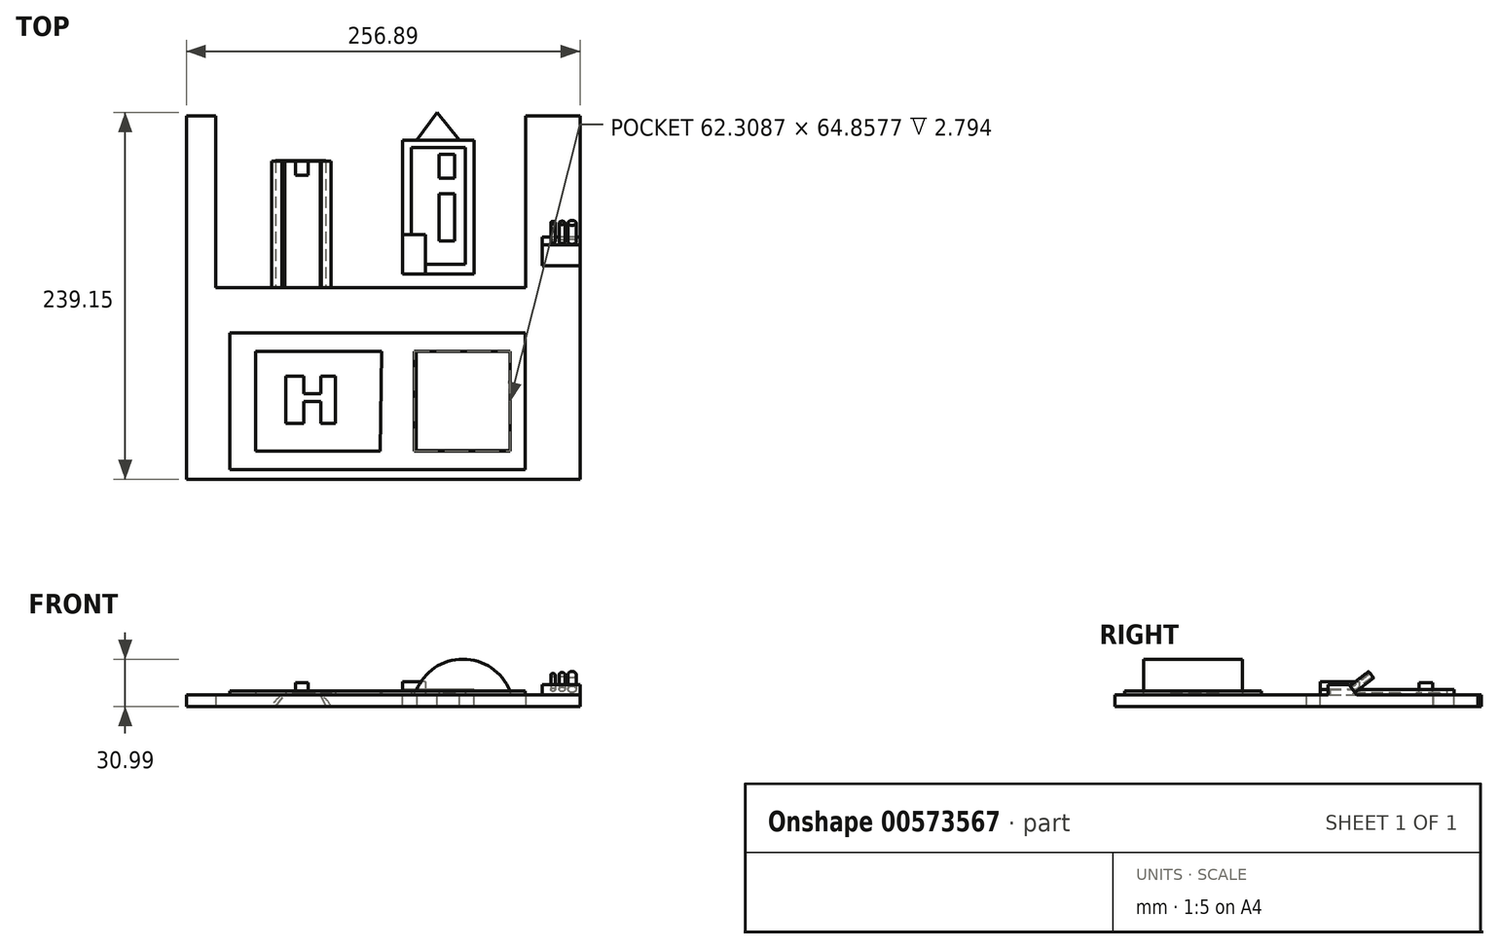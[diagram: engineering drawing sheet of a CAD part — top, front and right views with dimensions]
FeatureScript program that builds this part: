
annotation { "Feature Type Name" : "Feature", "Feature Type Description" : "" }
export const myFeature = defineFeature(function(context is Context, id is Id, definition is map)
    precondition{}
    {
        {
            var Q0;
            Q0=qCreatedBy(makeId("Top.planeOp"),FACE);
            var sketch = newSketch(context, id + "F0", { "sketchPlane" : qUnion([Q0])});
            skLineSegment(sketch, "E0.bottom", {"start": v(-141.19, 57.64) * mm, "end": v(115.7, 57.64) * mm});
            skLineSegment(sketch, "E0.top", {"start": v(-141.19, -67.27) * mm, "end": v(115.7, -67.27) * mm});
            skLineSegment(sketch, "E0.left", {"start": v(-141.19, 57.64) * mm, "end": v(-141.19, -67.27) * mm});
            skLineSegment(sketch, "E0.right", {"start": v(115.7, 57.64) * mm, "end": v(115.7, -67.27) * mm});
            skSolve(sketch);
        }
        {
            var Q0;
            Q0 = qSketchRegion(id + "F0", true);
            extrude(context, id + "F1", {"entities" : qUnion([Q0]), "depth" : 7.37 * mm, "offsetDistance" : 25.4 * mm});
        }
        {
            var Q0;
            Q0=makeQuery(id+"F1.opExtrude","CAP_FACE",FACE,{"disambiguationData":[OSD([sQuery(id+"F0.wireOp",EDGE,"E0.bottom"),sQuery(id+"F0.wireOp",EDGE,"E0.top"),sQuery(id+"F0.wireOp",EDGE,"E0.left"),sQuery(id+"F0.wireOp",EDGE,"E0.right")])],"isStart":false});
            var sketch = newSketch(context, id + "F2", { "sketchPlane" : qUnion([Q0])});
            skLineSegment(sketch, "E1", {"start": v(-13.88, 16) * mm, "end": v(-96.01, 16) * mm});
            skLineSegment(sketch, "E2", {"start": v(-96.01, 16) * mm, "end": v(-96.01, -48.86) * mm});
            skLineSegment(sketch, "E3", {"start": v(-96.01, -48.86) * mm, "end": v(-14.73, -48.86) * mm});
            skLineSegment(sketch, "E4", {"start": v(-14.73, -48.86) * mm, "end": v(-13.88, 16) * mm});
            skLineSegment(sketch, "E5", {"start": v(-13.88, -61.03) * mm, "end": v(-112.72, -61.03) * mm});
            skLineSegment(sketch, "E6", {"start": v(-112.72, -61.03) * mm, "end": v(-112.72, 28.18) * mm});
            skLineSegment(sketch, "E7", {"start": v(-112.72, 28.18) * mm, "end": v(-13.88, 28.18) * mm});
            skLineSegment(sketch, "E8", {"start": v(-13.88, 28.18) * mm, "end": v(79.87, 28.18) * mm});
            skLineSegment(sketch, "E9", {"start": v(79.87, 28.18) * mm, "end": v(79.87, -61.03) * mm});
            skLineSegment(sketch, "E10", {"start": v(79.87, -61.03) * mm, "end": v(-13.88, -61.03) * mm});
            skLineSegment(sketch, "E11", {"start": v(7.65, 16) * mm, "end": v(7.65, -48.86) * mm});
            skLineSegment(sketch, "E12", {"start": v(7.65, -48.86) * mm, "end": v(69.96, -48.86) * mm});
            skLineSegment(sketch, "E13", {"start": v(69.96, -48.86) * mm, "end": v(69.96, 16) * mm});
            skLineSegment(sketch, "E14", {"start": v(69.96, 16) * mm, "end": v(7.65, 16) * mm});
            skSolve(sketch);
        }
        {
            var Q0;
            Q0 = qSketchRegion(id + "F2", true);
            extrude(context, id + "F3", {"entities" : qUnion([Q0]), "operationType" : NewBodyOperationType.ADD, "depth" : 2.8 * mm, "offsetDistance" : 25.4 * mm});
        }
        {
            var Q0;
            Q0=makeQuery(id+"F3.boolean.opBoolean","SPLIT",FACE,{"disambiguationData":[TD([makeQuery(id+"F3.opExtrude","SWEPT_FACE",FACE,{"disambiguationData":[OSD([sQuery(id+"F2.wireOp",EDGE,"E1")])]})])],"derivedFrom":makeQuery(id+"F1.opExtrude","CAP_FACE",FACE,{"disambiguationData":[OSD([sQuery(id+"F0.wireOp",EDGE,"E0.bottom"),sQuery(id+"F0.wireOp",EDGE,"E0.top"),sQuery(id+"F0.wireOp",EDGE,"E0.left"),sQuery(id+"F0.wireOp",EDGE,"E0.right")])],"isStart":false})});
            var sketch = newSketch(context, id + "F4", { "sketchPlane" : qUnion([Q0])});
            skLineSegment(sketch, "E15", {"start": v(-76.23, 0) * mm, "end": v(-76.23, -30.71) * mm});
            skLineSegment(sketch, "E16", {"start": v(-76.23, -30.71) * mm, "end": v(-64.56, -30.71) * mm});
            skLineSegment(sketch, "E17", {"start": v(-64.56, -30.71) * mm, "end": v(-64.56, -16.64) * mm});
            skLineSegment(sketch, "E18", {"start": v(-64.56, -16.64) * mm, "end": v(-53.58, -16.64) * mm});
            skLineSegment(sketch, "E19", {"start": v(-53.58, -16.64) * mm, "end": v(-53.58, -30.71) * mm});
            skLineSegment(sketch, "E20", {"start": v(-53.58, -30.71) * mm, "end": v(-43.97, -30.71) * mm});
            skLineSegment(sketch, "E21", {"start": v(-43.97, -30.71) * mm, "end": v(-43.97, 0) * mm});
            skLineSegment(sketch, "E22", {"start": v(-43.97, 0) * mm, "end": v(-53.58, 0) * mm});
            skLineSegment(sketch, "E23", {"start": v(-53.58, 0) * mm, "end": v(-53.58, -11.5) * mm});
            skLineSegment(sketch, "E24", {"start": v(-53.58, -11.5) * mm, "end": v(-64.56, -11.5) * mm});
            skLineSegment(sketch, "E25", {"start": v(-64.56, -11.5) * mm, "end": v(-64.56, 0) * mm});
            skLineSegment(sketch, "E26", {"start": v(-64.56, 0) * mm, "end": v(-76.23, 0) * mm});
            skSolve(sketch);
        }
        {
            var Q0;
            Q0 = qSketchRegion(id + "F4", true);
            extrude(context, id + "F5", {"entities" : qUnion([Q0]), "operationType" : NewBodyOperationType.ADD, "depth" : 1.78 * mm, "offsetDistance" : 25.4 * mm});
        }
        {
            var Q0;
            Q0=makeQuery(id+"F3.opExtrude","SWEPT_FACE",FACE,{"disambiguationData":[OSD([sQuery(id+"F2.wireOp",EDGE,"E14")])]});
            var sketch = newSketch(context, id + "F6", { "sketchPlane" : qUnion([Q0])});
            skArc(sketch, "E27", {"start": v(69.96, 10.16) * mm, "mid": v(37.82, 30.7) * mm, "end": v(7.65, 7.37) * mm});
            skSolve(sketch);
        }
        {
            var Q0;
            {var subQ0=sQuery(id+"F6.wireOp",EDGE,"E27");var subQ1=sQuery(id+"F2.wireOp",EDGE,"E14");var subQ2=makeQuery(id+"F3.opExtrude","CAP_EDGE",EDGE,{"disambiguationData":[OSD([subQ1])],"isStart":false});var subQ4=makeQuery(id+"F6.imprint","INTERSECT",VERTEX,{"derivedFrom":[subQ2,subQ0]});Q0=makeQuery(id+"F6.imprint","IMPRINT",FACE,{"disambiguationData":[TD([[makeQuery(id+"F6.imprint","IMPRINT",EDGE,{"disambiguationData":[TD([[subQ4,1.0]])],"derivedFrom":subQ0}),1.0]])]});}
            extrude(context, id + "F7", {"entities" : qUnion([Q0]), "depth" : 64.52 * mm, "offsetDistance" : 25.4 * mm});
        }
        {
            var Q0;
            Q0=makeQuery(id+"F1.opExtrude","SWEPT_FACE",FACE,{"disambiguationData":[OSD([sQuery(id+"F0.wireOp",EDGE,"E0.bottom")])]});
            var sketch = newSketch(context, id + "F8", { "sketchPlane" : qUnion([Q0])});
            skLineSegment(sketch, "E28.bottom", {"start": v(-80.15, 7.37) * mm, "end": v(-115.7, 7.37) * mm});
            skLineSegment(sketch, "E28.top", {"start": v(-80.15, 0) * mm, "end": v(-115.7, 0) * mm});
            skLineSegment(sketch, "E28.left", {"start": v(-80.15, 7.37) * mm, "end": v(-80.15, 0) * mm});
            skLineSegment(sketch, "E28.right", {"start": v(-115.7, 7.37) * mm, "end": v(-115.7, 0) * mm});
            skLineSegment(sketch, "E29.bottom", {"start": v(141.19, 7.37) * mm, "end": v(122.07, 7.37) * mm});
            skLineSegment(sketch, "E29.top", {"start": v(141.19, 0) * mm, "end": v(122.07, 0) * mm});
            skLineSegment(sketch, "E29.left", {"start": v(141.19, 7.37) * mm, "end": v(141.19, 0) * mm});
            skLineSegment(sketch, "E29.right", {"start": v(122.07, 7.37) * mm, "end": v(122.07, 0) * mm});
            skSolve(sketch);
        }
        {
            var Q0;
            Q0 = qSketchRegion(id + "F8", true);
            extrude(context, id + "F9", {"entities" : qUnion([Q0]), "operationType" : NewBodyOperationType.ADD, "depth" : 112.01 * mm, "offsetDistance" : 25.4 * mm});
        }
        {
            var Q0;
            {var subQ0=sQuery(id+"F0.wireOp",EDGE,"E0.left");var subQ1=sQuery(id+"F0.wireOp",EDGE,"E0.top");var subQ2=sQuery(id+"F0.wireOp",EDGE,"E0.right");var subQ3=sQuery(id+"F0.wireOp",EDGE,"E0.bottom");Q0=makeQuery(id+"F9.boolean.opBoolean","MERGE",FACE,{"derivedFrom":[makeQuery(id+"F3.boolean.opBoolean","SPLIT",FACE,{"disambiguationData":[TD([makeQuery(id+"F1.opExtrude","SWEPT_FACE",FACE,{"disambiguationData":[OSD([subQ3])]})])],"derivedFrom":makeQuery(id+"F1.opExtrude","CAP_FACE",FACE,{"disambiguationData":[OSD([subQ3,subQ1,subQ0,subQ2])],"isStart":false})}),makeQuery(id+"F9.opExtrude","SWEPT_FACE",FACE,{"disambiguationData":[OSD([sQuery(id+"F8.wireOp",EDGE,"E28.bottom")])]}),makeQuery(id+"F9.opExtrude","SWEPT_FACE",FACE,{"disambiguationData":[OSD([sQuery(id+"F8.wireOp",EDGE,"E29.bottom")])]})]});}
            var sketch = newSketch(context, id + "F10", { "sketchPlane" : qUnion([Q0])});
            skLineSegment(sketch, "E30.bottom", {"start": v(46.65, 153.87) * mm, "end": v(0, 153.87) * mm});
            skLineSegment(sketch, "E30.top", {"start": v(46.65, 66.6) * mm, "end": v(0, 66.6) * mm});
            skLineSegment(sketch, "E30.left", {"start": v(46.65, 153.87) * mm, "end": v(46.65, 66.6) * mm});
            skLineSegment(sketch, "E30.right", {"start": v(0, 153.87) * mm, "end": v(0, 66.6) * mm});
            skSolve(sketch);
        }
        {
            var Q0;
            Q0 = qSketchRegion(id + "F10", true);
            extrude(context, id + "F11", {"entities" : qUnion([Q0]), "oppositeDirection" : true, "depth" : 7.62 * mm, "offsetDistance" : 25.4 * mm});
        }
        {
            var Q0;
            Q0=makeQuery(id+"F11.opExtrude","CAP_FACE",FACE,{"disambiguationData":[OSD([sQuery(id+"F10.wireOp",EDGE,"E30.bottom"),sQuery(id+"F10.wireOp",EDGE,"E30.top"),sQuery(id+"F10.wireOp",EDGE,"E30.left"),sQuery(id+"F10.wireOp",EDGE,"E30.right")])],"isStart":true});
            var sketch = newSketch(context, id + "F12", { "sketchPlane" : qUnion([Q0])});
            skLineSegment(sketch, "E31.bottom", {"start": v(33.86, 144.73) * mm, "end": v(23.8, 144.73) * mm});
            skLineSegment(sketch, "E31.top", {"start": v(33.86, 129.2) * mm, "end": v(23.8, 129.2) * mm});
            skLineSegment(sketch, "E31.left", {"start": v(33.86, 144.73) * mm, "end": v(33.86, 129.2) * mm});
            skLineSegment(sketch, "E31.right", {"start": v(23.8, 144.73) * mm, "end": v(23.8, 129.2) * mm});
            skLineSegment(sketch, "E32.bottom", {"start": v(33.86, 119.14) * mm, "end": v(23.8, 119.14) * mm});
            skLineSegment(sketch, "E32.top", {"start": v(33.86, 88.07) * mm, "end": v(23.8, 88.07) * mm});
            skLineSegment(sketch, "E32.left", {"start": v(33.86, 119.14) * mm, "end": v(33.86, 88.07) * mm});
            skLineSegment(sketch, "E32.right", {"start": v(23.8, 119.14) * mm, "end": v(23.8, 88.07) * mm});
            skSolve(sketch);
        }
        {
            var Q0;
            Q0 = qSketchRegion(id + "F12", true);
            extrude(context, id + "F13", {"entities" : qUnion([Q0]), "operationType" : NewBodyOperationType.ADD, "depth" : 1.27 * mm, "offsetDistance" : 25.4 * mm});
        }
        {
            var Q0;
            Q0=makeQuery(id+"F11.opExtrude","CAP_FACE",FACE,{"disambiguationData":[OSD([sQuery(id+"F10.wireOp",EDGE,"E30.bottom"),sQuery(id+"F10.wireOp",EDGE,"E30.top"),sQuery(id+"F10.wireOp",EDGE,"E30.left"),sQuery(id+"F10.wireOp",EDGE,"E30.right")])],"isStart":true});
            var sketch = newSketch(context, id + "F14", { "sketchPlane" : qUnion([Q0])});
            skLineSegment(sketch, "E33.bottom", {"start": v(14.67, 66.6) * mm, "end": v(0, 66.6) * mm});
            skLineSegment(sketch, "E33.top", {"start": v(14.67, 92.19) * mm, "end": v(0, 92.19) * mm});
            skLineSegment(sketch, "E33.left", {"start": v(14.67, 66.6) * mm, "end": v(14.67, 92.19) * mm});
            skLineSegment(sketch, "E33.right", {"start": v(0, 66.6) * mm, "end": v(0, 92.19) * mm});
            skSolve(sketch);
        }
        {
            var Q0;
            Q0 = qSketchRegion(id + "F14", true);
            extrude(context, id + "F15", {"entities" : qUnion([Q0]), "operationType" : NewBodyOperationType.ADD, "depth" : 8.64 * mm, "offsetDistance" : 25.4 * mm});
        }
        {
            var Q0;
            Q0=makeQuery(id+"F11.opExtrude","CAP_FACE",FACE,{"disambiguationData":[OSD([sQuery(id+"F10.wireOp",EDGE,"E30.bottom"),sQuery(id+"F10.wireOp",EDGE,"E30.top"),sQuery(id+"F10.wireOp",EDGE,"E30.left"),sQuery(id+"F10.wireOp",EDGE,"E30.right")])],"isStart":true});
            var sketch = newSketch(context, id + "F16", { "sketchPlane" : qUnion([Q0])});
            skLineSegment(sketch, "E34", {"start": v(0, 92.19) * mm, "end": v(0, 153.87) * mm});
            skLineSegment(sketch, "E35", {"start": v(0, 153.87) * mm, "end": v(46.65, 153.87) * mm});
            skLineSegment(sketch, "E36", {"start": v(46.65, 153.87) * mm, "end": v(46.65, 66.6) * mm});
            skLineSegment(sketch, "E37", {"start": v(46.65, 66.6) * mm, "end": v(14.67, 66.6) * mm});
            skLineSegment(sketch, "E38", {"start": v(14.67, 66.6) * mm, "end": v(14.67, 73) * mm});
            skLineSegment(sketch, "E39", {"start": v(14.67, 73) * mm, "end": v(40.71, 73) * mm});
            skLineSegment(sketch, "E40", {"start": v(40.71, 73) * mm, "end": v(40.71, 149.3) * mm});
            skLineSegment(sketch, "E41", {"start": v(40.71, 149.3) * mm, "end": v(5.53, 149.3) * mm});
            skLineSegment(sketch, "E42", {"start": v(5.53, 149.3) * mm, "end": v(5.53, 92.19) * mm});
            skLineSegment(sketch, "E43", {"start": v(5.53, 92.19) * mm, "end": v(0, 92.19) * mm});
            skSolve(sketch);
        }
        {
            var Q0;
            Q0 = qSketchRegion(id + "F16", true);
            extrude(context, id + "F17", {"entities" : qUnion([Q0]), "operationType" : NewBodyOperationType.ADD, "depth" : 3.56 * mm, "offsetDistance" : 25.4 * mm});
        }
        {
            var Q0;
            Q0=makeQuery(id+"F11.opExtrude","CAP_FACE",FACE,{"disambiguationData":[OSD([sQuery(id+"F10.wireOp",EDGE,"E30.bottom"),sQuery(id+"F10.wireOp",EDGE,"E30.top"),sQuery(id+"F10.wireOp",EDGE,"E30.left"),sQuery(id+"F10.wireOp",EDGE,"E30.right")])],"isStart":true});
            var sketch = newSketch(context, id + "F18", { "sketchPlane" : qUnion([Q0])});
            skLineSegment(sketch, "E44", {"start": v(5.53, 149.3) * mm, "end": v(22.4, 171.88) * mm});
            skLineSegment(sketch, "E45", {"start": v(22.4, 171.88) * mm, "end": v(40.71, 149.3) * mm});
            skLineSegment(sketch, "E46", {"start": v(40.71, 149.3) * mm, "end": v(5.53, 149.3) * mm});
            skSolve(sketch);
        }
        {
            var Q0;
            Q0 = qSketchRegion(id + "F18", true);
            extrude(context, id + "F19", {"entities" : qUnion([Q0]), "operationType" : NewBodyOperationType.ADD, "oppositeDirection" : true, "depth" : 7.37 * mm, "offsetDistance" : 25.4 * mm});
        }
        {
            var Q0;
            Q0=makeQuery(id+"F1.opExtrude","SWEPT_FACE",FACE,{"disambiguationData":[OSD([sQuery(id+"F0.wireOp",EDGE,"E0.bottom")])]});
            var sketch = newSketch(context, id + "F20", { "sketchPlane" : qUnion([Q0])});
            skArc(sketch, "E47", {"start": v(85.5, 0) * mm, "mid": v(66.1, 11.5) * mm, "end": v(46.72, 0) * mm});
            skSolve(sketch);
        }
        {
            var Q0;
            {var subQ0=sQuery(id+"F20.wireOp",EDGE,"E47");var subQ1=makeQuery(id+"F1.opExtrude","CAP_EDGE",EDGE,{"disambiguationData":[OSD([sQuery(id+"F0.wireOp",EDGE,"E0.bottom")])],"isStart":false});var subQ2=makeQuery(id+"F20.imprint","INTERSECT",VERTEX,{"disambiguationData":[OD(0.0)],"derivedFrom":[subQ1,subQ0]});Q0=makeQuery(id+"F20.imprint","IMPRINT",FACE,{"disambiguationData":[TD([[makeQuery(id+"F20.imprint","IMPRINT",EDGE,{"disambiguationData":[TD([[subQ2,-1.0]])],"derivedFrom":subQ0}),1.0]])]});}
            extrude(context, id + "F21", {"entities" : qUnion([Q0]), "depth" : 82.55 * mm, "offsetDistance" : 25.4 * mm});
        }
        {
            var Q0;
            Q0=makeQuery(id+"F1.opExtrude","SWEPT_FACE",FACE,{"disambiguationData":[OSD([sQuery(id+"F0.wireOp",EDGE,"E0.bottom")])]});
            var sketch = newSketch(context, id + "F22", { "sketchPlane" : qUnion([Q0])});
            skLineSegment(sketch, "E48", {"start": v(53.92, 7.37) * mm, "end": v(50.15, 0) * mm});
            skLineSegment(sketch, "E49", {"start": v(50.15, 0) * mm, "end": v(83.1, 0) * mm});
            skLineSegment(sketch, "E50", {"start": v(83.1, 0) * mm, "end": v(76.92, 7.37) * mm});
            skLineSegment(sketch, "E51", {"start": v(76.92, 7.37) * mm, "end": v(53.92, 7.37) * mm});
            skSolve(sketch);
        }
        {
            var Q0;
            Q0=makeQuery(id+"F22.imprint","IMPRINT",FACE,{"disambiguationData":[TD([[makeQuery(id+"F22.imprint","IMPRINT",EDGE,{"derivedFrom":sQuery(id+"F22.wireOp",EDGE,"E48")}),1.0]])]});
            extrude(context, id + "F23", {"entities" : qUnion([Q0]), "depth" : 82.8 * mm, "offsetDistance" : 25.4 * mm});
        }
        {
            var Q0;
            Q0=makeQuery(id+"F21.opExtrude","CAP_FACE",FACE,{"disambiguationData":[OSD([sQuery(id+"F0.wireOp",EDGE,"E0.bottom"),sQuery(id+"F20.wireOp",EDGE,"E47")])],"isStart":false});
            var sketch = newSketch(context, id + "F24", { "sketchPlane" : qUnion([Q0])});
            skLineSegment(sketch, "E52.bottom", {"start": v(61.82, 7.37) * mm, "end": v(70.05, 7.37) * mm});
            skLineSegment(sketch, "E52.top", {"start": v(61.82, 15.27) * mm, "end": v(70.05, 15.27) * mm});
            skLineSegment(sketch, "E52.left", {"start": v(61.82, 7.37) * mm, "end": v(61.82, 15.27) * mm});
            skLineSegment(sketch, "E52.right", {"start": v(70.05, 7.37) * mm, "end": v(70.05, 15.27) * mm});
            skSolve(sketch);
        }
        {
            var Q0;
            Q0 = qSketchRegion(id + "F24", true);
            extrude(context, id + "F25", {"entities" : qUnion([Q0]), "oppositeDirection" : true, "depth" : 9.14 * mm, "offsetDistance" : 25.4 * mm});
        }
        {
            var Q0;
            Q0=makeQuery(id+"F9.boolean.opBoolean","MERGE",FACE,{"derivedFrom":[makeQuery(id+"F1.opExtrude","SWEPT_FACE",FACE,{"disambiguationData":[OSD([sQuery(id+"F0.wireOp",EDGE,"E0.right")])]}),makeQuery(id+"F9.opExtrude","SWEPT_FACE",FACE,{"disambiguationData":[OSD([sQuery(id+"F8.wireOp",EDGE,"E28.right")])]})]});
            var sketch = newSketch(context, id + "F26", { "sketchPlane" : qUnion([Q0])});
            skLineSegment(sketch, "E53", {"start": v(96.27, 0) * mm, "end": v(85.5, 14.02) * mm});
            skLineSegment(sketch, "E54", {"start": v(85.5, 14.02) * mm, "end": v(71.91, 14.02) * mm});
            skLineSegment(sketch, "E55", {"start": v(71.91, 14.02) * mm, "end": v(71.91, 0) * mm});
            skLineSegment(sketch, "E56", {"start": v(71.91, 0) * mm, "end": v(96.27, 0) * mm});
            skSolve(sketch);
        }
        {
            var Q0;
            Q0 = qSketchRegion(id + "F26", true);
            extrude(context, id + "F27", {"entities" : qUnion([Q0]), "operationType" : NewBodyOperationType.ADD, "oppositeDirection" : true, "depth" : 24.64 * mm, "offsetDistance" : 25.4 * mm});
        }
        {
            var Q0;
            Q0=makeQuery(id+"F27.opExtrude","SWEPT_FACE",FACE,{"disambiguationData":[OSD([sQuery(id+"F26.wireOp",EDGE,"E53")])]});
            var sketch = newSketch(context, id + "F28", { "sketchPlane" : qUnion([Q0])});
            skCircle(sketch, "E57", {"center": v(-110.46, -44.52) * mm, "radius": 2.68 * mm});
            skCircle(sketch, "E58", {"center": v(-98, -44.88) * mm, "radius": 1.43 * mm});
            skCircle(sketch, "E59", {"center": v(-103.94, -44.52) * mm, "radius": 1.87 * mm});
            skSolve(sketch);
        }
        {
            var Q0;
            Q0 = qSketchRegion(id + "F28", true);
            extrude(context, id + "F29", {"entities" : qUnion([Q0]), "operationType" : NewBodyOperationType.ADD, "depth" : 15.5 * mm, "offsetDistance" : 25.4 * mm});
        }
    });
